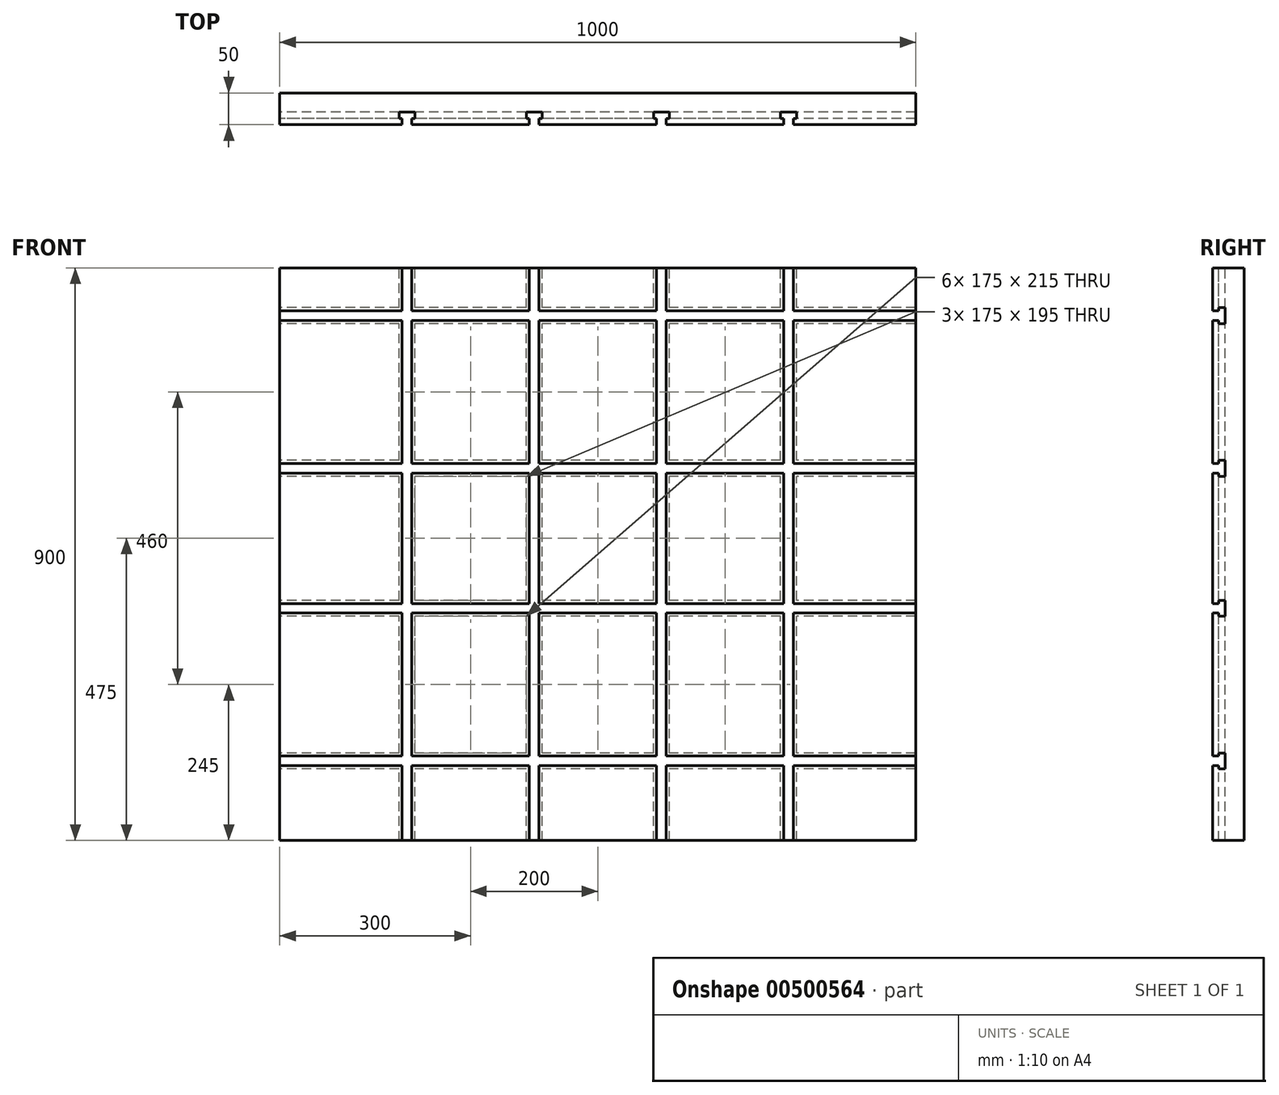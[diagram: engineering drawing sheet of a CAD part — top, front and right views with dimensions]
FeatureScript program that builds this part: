
annotation { "Feature Type Name" : "Feature", "Feature Type Description" : "" }
export const myFeature = defineFeature(function(context is Context, id is Id, definition is map)
    precondition{}
    {
        {
            var Q0;
            Q0=qCreatedBy(makeId("Front.planeOp"),FACE);
            var sketch = newSketch(context, id + "F0", { "sketchPlane" : qUnion([Q0])});
            skLineSegment(sketch, "E0.bottom", {"start": v(-500, -450) * mm, "end": v(500, -450) * mm});
            skLineSegment(sketch, "E0.top", {"start": v(-500, 450) * mm, "end": v(500, 450) * mm});
            skLineSegment(sketch, "E0.left", {"start": v(-500, -450) * mm, "end": v(-500, 450) * mm});
            skLineSegment(sketch, "E0.right", {"start": v(500, -450) * mm, "end": v(500, 450) * mm});
            skPoint(sketch, "E0.middle", {"position": v(0, 0) * mm});
            skSolve(sketch);
        }
        {
            var Q0;
            Q0=makeQuery(id+"F0.imprint","IMPRINT",FACE,{"disambiguationData":[TD([[makeQuery(id+"F0.imprint","IMPRINT",EDGE,{"derivedFrom":sQuery(id+"F0.wireOp",EDGE,"E0.bottom")}),1.0]])]});
            extrude(context, id + "F1", {"entities" : qUnion([Q0]), "depth" : 50 * mm});
        }
        {
            var Q0;
            Q0=makeQuery(id+"F1.opExtrude","SWEPT_FACE",FACE,{"disambiguationData":[OSD([sQuery(id+"F0.wireOp",EDGE,"E0.left")])]});
            var sketch = newSketch(context, id + "F2", { "sketchPlane" : qUnion([Q0])});
            skLineSegment(sketch, "E1.bottom", {"start": v(50, -317.5) * mm, "end": v(40, -317.5) * mm});
            skLineSegment(sketch, "E1.top", {"start": v(50, -332.5) * mm, "end": v(40, -332.5) * mm});
            skLineSegment(sketch, "E1.left", {"start": v(50, -317.5) * mm, "end": v(50, -332.5) * mm});
            skLineSegment(sketch, "E2.bottom", {"start": v(40, -312.5) * mm, "end": v(30, -312.5) * mm});
            skLineSegment(sketch, "E2.top", {"start": v(40, -337.5) * mm, "end": v(30, -337.5) * mm});
            skLineSegment(sketch, "E2.left", {"start": v(40, -312.5) * mm, "end": v(40, -317.5) * mm});
            skLineSegment(sketch, "E2.right", {"start": v(30, -312.5) * mm, "end": v(30, -337.5) * mm});
            skLineSegment(sketch, "E3.MirrorCS", {"start": v(40, -97.5) * mm, "end": v(30, -97.5) * mm});
            skLineSegment(sketch, "E4.MirrorCS", {"start": v(30, -97.5) * mm, "end": v(30, -72.5) * mm});
            skLineSegment(sketch, "E5.MirrorCS", {"start": v(40, -97.5) * mm, "end": v(40, -92.5) * mm});
            skLineSegment(sketch, "E6.MirrorCS", {"start": v(50, -92.5) * mm, "end": v(40, -92.5) * mm});
            skLineSegment(sketch, "E7.MirrorCS", {"start": v(50, -92.5) * mm, "end": v(50, -77.5) * mm});
            skLineSegment(sketch, "E8.MirrorCS", {"start": v(50, -77.5) * mm, "end": v(40, -77.5) * mm});
            skLineSegment(sketch, "E9.MirrorCS", {"start": v(40, -72.5) * mm, "end": v(30, -72.5) * mm});
            skLineSegment(sketch, "E10.MirrorCS", {"start": v(40, 122.5) * mm, "end": v(30, 122.5) * mm});
            skLineSegment(sketch, "E11.MirrorCS", {"start": v(30, 147.5) * mm, "end": v(30, 122.5) * mm});
            skLineSegment(sketch, "E12.MirrorCS", {"start": v(40, 147.5) * mm, "end": v(40, 142.5) * mm});
            skLineSegment(sketch, "E13.MirrorCS", {"start": v(50, 142.5) * mm, "end": v(50, 127.5) * mm});
            skLineSegment(sketch, "E14.MirrorCS", {"start": v(40, 147.5) * mm, "end": v(30, 147.5) * mm});
            skLineSegment(sketch, "E15.MirrorCS", {"start": v(50, 127.5) * mm, "end": v(40, 127.5) * mm});
            skLineSegment(sketch, "E16", {"start": v(50, 142.5) * mm, "end": v(40, 142.5) * mm});
            skLineSegment(sketch, "E17.MirrorCS", {"start": v(40, 362.5) * mm, "end": v(30, 362.5) * mm});
            skLineSegment(sketch, "E18.MirrorCS", {"start": v(30, 362.5) * mm, "end": v(30, 387.5) * mm});
            skLineSegment(sketch, "E19.MirrorCS", {"start": v(40, 387.5) * mm, "end": v(30, 387.5) * mm});
            skLineSegment(sketch, "E20.MirrorCS", {"start": v(50, 382.5) * mm, "end": v(40, 382.5) * mm});
            skLineSegment(sketch, "E21.MirrorCS", {"start": v(50, 367.5) * mm, "end": v(50, 382.5) * mm});
            skLineSegment(sketch, "E22.MirrorCS", {"start": v(50, 367.5) * mm, "end": v(40, 367.5) * mm});
            skLineSegment(sketch, "E23.MirrorCS", {"start": v(40, 362.5) * mm, "end": v(40, 367.5) * mm});
            skLineSegment(sketch, "E24", {"start": v(40, 382.5) * mm, "end": v(40, 387.5) * mm});
            skLineSegment(sketch, "E25", {"start": v(40, 142.5) * mm, "end": v(40, 142.5) * mm});
            skLineSegment(sketch, "E26", {"start": v(40, 127.5) * mm, "end": v(40, 127.5) * mm});
            skLineSegment(sketch, "E27", {"start": v(40, 127.5) * mm, "end": v(40, 122.5) * mm});
            skLineSegment(sketch, "E28", {"start": v(40, -77.5) * mm, "end": v(40, -72.5) * mm});
            skLineSegment(sketch, "E29", {"start": v(40, -317.5) * mm, "end": v(40, -317.5) * mm});
            skLineSegment(sketch, "E30", {"start": v(40, -332.5) * mm, "end": v(40, -337.5) * mm});
            skSolve(sketch);
        }
        {
            var Q0;
            Q0=makeQuery(id+"F2.imprint","IMPRINT",FACE,{"disambiguationData":[TD([[makeQuery(id+"F2.imprint","IMPRINT",EDGE,{"derivedFrom":sQuery(id+"F2.wireOp",EDGE,"E1.bottom")}),1.0]])]});
            var Q1;
            Q1=makeQuery(id+"F2.imprint","IMPRINT",FACE,{"disambiguationData":[TD([[makeQuery(id+"F2.imprint","IMPRINT",EDGE,{"derivedFrom":sQuery(id+"F2.wireOp",EDGE,"E3.MirrorCS")}),-1.0]])]});
            var Q2;
            Q2=makeQuery(id+"F2.imprint","IMPRINT",FACE,{"disambiguationData":[TD([[makeQuery(id+"F2.imprint","IMPRINT",EDGE,{"derivedFrom":sQuery(id+"F2.wireOp",EDGE,"E10.MirrorCS")}),-1.0]])]});
            var Q3;
            Q3=makeQuery(id+"F2.imprint","IMPRINT",FACE,{"disambiguationData":[TD([[makeQuery(id+"F2.imprint","IMPRINT",EDGE,{"derivedFrom":sQuery(id+"F2.wireOp",EDGE,"E17.MirrorCS")}),-1.0]])]});
            extrude(context, id + "F3", {"entities" : qUnion([Q0, Q1, Q2, Q3]), "operationType" : NewBodyOperationType.REMOVE, "oppositeDirection" : true, "depth" : 1016 * mm});
        }
        {
            var Q0;
            Q0=makeQuery(id+"F1.opExtrude","SWEPT_FACE",FACE,{"disambiguationData":[OSD([sQuery(id+"F0.wireOp",EDGE,"E0.top")])]});
            var sketch = newSketch(context, id + "F4", { "sketchPlane" : qUnion([Q0])});
            skLineSegment(sketch, "E31.bottom", {"start": v(-307.5, -50) * mm, "end": v(-292.5, -50) * mm});
            skLineSegment(sketch, "E31.left", {"start": v(-307.5, -50) * mm, "end": v(-307.5, -40) * mm});
            skLineSegment(sketch, "E31.right", {"start": v(-292.5, -50) * mm, "end": v(-292.5, -40) * mm});
            skLineSegment(sketch, "E32.bottom", {"start": v(-312.5, -40) * mm, "end": v(-307.5, -40) * mm});
            skLineSegment(sketch, "E32.top", {"start": v(-312.5, -30) * mm, "end": v(-287.5, -30) * mm});
            skLineSegment(sketch, "E32.left", {"start": v(-312.5, -40) * mm, "end": v(-312.5, -30) * mm});
            skLineSegment(sketch, "E32.right", {"start": v(-287.5, -40) * mm, "end": v(-287.5, -30) * mm});
            skLineSegment(sketch, "E33.MirrorCS", {"start": v(-112.5, -40) * mm, "end": v(-112.5, -30) * mm});
            skLineSegment(sketch, "E34.MirrorCS", {"start": v(-87.5, -30) * mm, "end": v(-112.5, -30) * mm});
            skLineSegment(sketch, "E35.MirrorCS", {"start": v(-87.5, -40) * mm, "end": v(-87.5, -30) * mm});
            skLineSegment(sketch, "E36.MirrorCS", {"start": v(-87.5, -40) * mm, "end": v(-92.5, -40) * mm});
            skLineSegment(sketch, "E37.MirrorCS", {"start": v(-92.5, -50) * mm, "end": v(-92.5, -40) * mm});
            skLineSegment(sketch, "E38.MirrorCS", {"start": v(-92.5, -50) * mm, "end": v(-107.5, -50) * mm});
            skLineSegment(sketch, "E39.MirrorCS", {"start": v(-107.5, -50) * mm, "end": v(-107.5, -40) * mm});
            skLineSegment(sketch, "E40.MirrorCS", {"start": v(87.5, -40) * mm, "end": v(87.5, -30) * mm});
            skLineSegment(sketch, "E41.MirrorCS", {"start": v(112.5, -30) * mm, "end": v(87.5, -30) * mm});
            skLineSegment(sketch, "E42.MirrorCS", {"start": v(112.5, -40) * mm, "end": v(112.5, -30) * mm});
            skLineSegment(sketch, "E43.MirrorCS", {"start": v(112.5, -40) * mm, "end": v(107.5, -40) * mm});
            skLineSegment(sketch, "E44.MirrorCS", {"start": v(92.5, -50) * mm, "end": v(92.5, -40) * mm});
            skLineSegment(sketch, "E45.MirrorCS", {"start": v(107.5, -50) * mm, "end": v(107.5, -40) * mm});
            skLineSegment(sketch, "E46.MirrorCS", {"start": v(107.5, -50) * mm, "end": v(92.5, -50) * mm});
            skLineSegment(sketch, "E47.MirrorCS", {"start": v(287.5, -40) * mm, "end": v(287.5, -30) * mm});
            skLineSegment(sketch, "E48.MirrorCS", {"start": v(287.5, -30) * mm, "end": v(312.5, -30) * mm});
            skLineSegment(sketch, "E49.MirrorCS", {"start": v(312.5, -40) * mm, "end": v(312.5, -30) * mm});
            skLineSegment(sketch, "E50.MirrorCS", {"start": v(287.5, -40) * mm, "end": v(292.5, -40) * mm});
            skLineSegment(sketch, "E51.MirrorCS", {"start": v(307.5, -50) * mm, "end": v(307.5, -40) * mm});
            skLineSegment(sketch, "E52.MirrorCS", {"start": v(292.5, -50) * mm, "end": v(307.5, -50) * mm});
            skLineSegment(sketch, "E53.MirrorCS", {"start": v(292.5, -50) * mm, "end": v(292.5, -40) * mm});
            skLineSegment(sketch, "E54", {"start": v(-292.5, -40) * mm, "end": v(-287.5, -40) * mm});
            skLineSegment(sketch, "E55", {"start": v(-107.5, -40) * mm, "end": v(-112.5, -40) * mm});
            skLineSegment(sketch, "E56", {"start": v(92.5, -40) * mm, "end": v(92.5, -40) * mm});
            skLineSegment(sketch, "E57", {"start": v(92.5, -40) * mm, "end": v(87.5, -40) * mm});
            skLineSegment(sketch, "E58", {"start": v(292.5, -40) * mm, "end": v(292.5, -40) * mm});
            skLineSegment(sketch, "E59", {"start": v(307.5, -40) * mm, "end": v(312.5, -40) * mm});
            skSolve(sketch);
        }
        {
            var Q0;
            Q0=makeQuery(id+"F4.imprint","IMPRINT",FACE,{"disambiguationData":[TD([[makeQuery(id+"F4.imprint","IMPRINT",EDGE,{"derivedFrom":sQuery(id+"F4.wireOp",EDGE,"E47.MirrorCS")}),-1.0]])]});
            var Q1;
            Q1=makeQuery(id+"F4.imprint","IMPRINT",FACE,{"disambiguationData":[TD([[makeQuery(id+"F4.imprint","IMPRINT",EDGE,{"derivedFrom":sQuery(id+"F4.wireOp",EDGE,"E40.MirrorCS")}),-1.0]])]});
            var Q2;
            Q2=makeQuery(id+"F4.imprint","IMPRINT",FACE,{"disambiguationData":[TD([[makeQuery(id+"F4.imprint","IMPRINT",EDGE,{"derivedFrom":sQuery(id+"F4.wireOp",EDGE,"E33.MirrorCS")}),-1.0]])]});
            var Q3;
            Q3=makeQuery(id+"F4.imprint","IMPRINT",FACE,{"disambiguationData":[TD([[makeQuery(id+"F4.imprint","IMPRINT",EDGE,{"derivedFrom":sQuery(id+"F4.wireOp",EDGE,"E31.bottom")}),1.0]])]});
            extrude(context, id + "F5", {"entities" : qUnion([Q0, Q1, Q2, Q3]), "operationType" : NewBodyOperationType.REMOVE, "oppositeDirection" : true, "depth" : 908 * mm});
        }
    });
